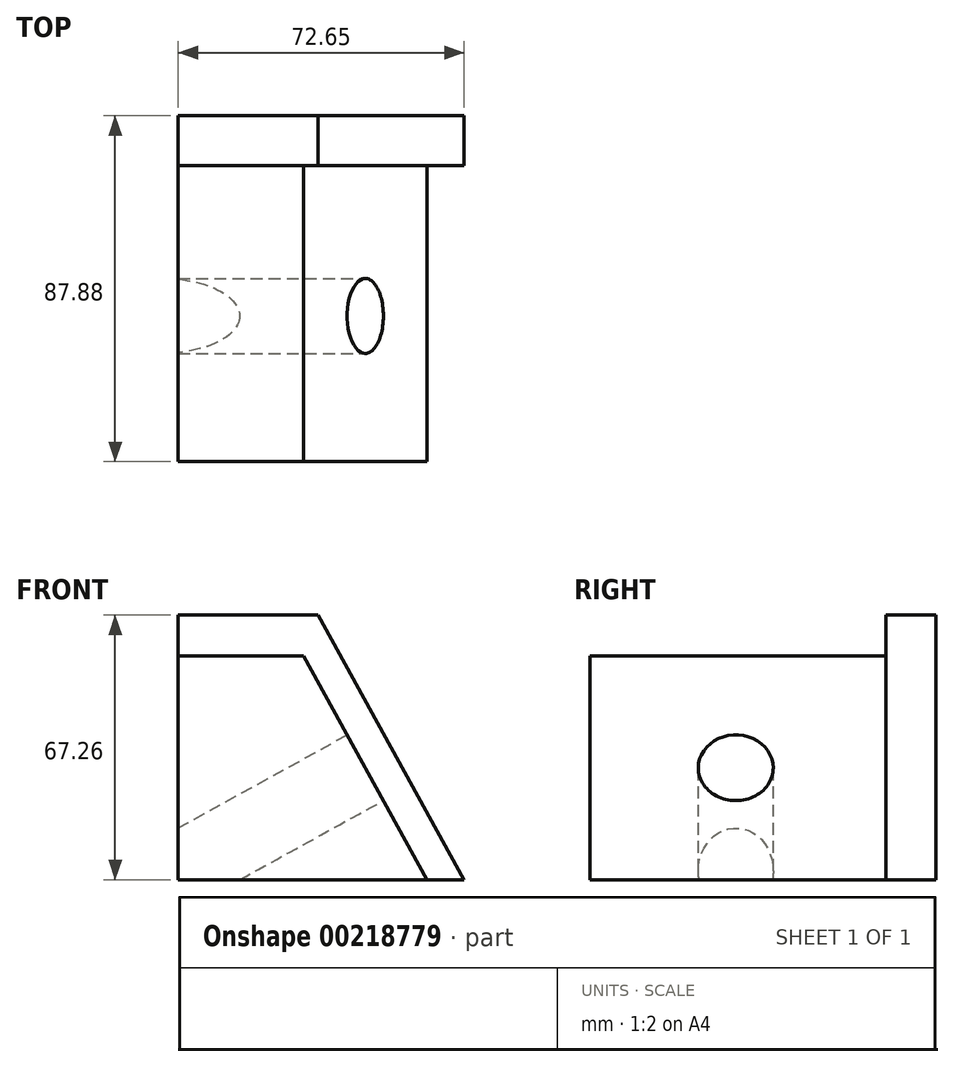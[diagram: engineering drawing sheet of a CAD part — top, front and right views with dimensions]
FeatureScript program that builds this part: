
annotation { "Feature Type Name" : "Feature", "Feature Type Description" : "" }
export const myFeature = defineFeature(function(context is Context, id is Id, definition is map)
    precondition{}
    {
        {
            var Q0;
            Q0=qCreatedBy(makeId("Front.planeOp"),FACE);
            var sketch = newSketch(context, id + "F0", { "sketchPlane" : qUnion([Q0])});
            skPoint(sketch, "E0.middle", {"position": v(0, 0) * mm});
            skLineSegment(sketch, "E1", {"start": v(-86.8, 0) * mm, "end": v(-86.8, 67.26) * mm});
            skLineSegment(sketch, "E2", {"start": v(-86.8, 67.26) * mm, "end": v(-51.25, 67.26) * mm});
            skLineSegment(sketch, "E3", {"start": v(-51.25, 67.26) * mm, "end": v(-14.16, 0) * mm});
            skLineSegment(sketch, "E4", {"start": v(-14.16, 0) * mm, "end": v(-86.8, 0) * mm});
            skSolve(sketch);
        }
        {
            var Q0;
            Q0=makeQuery(id+"F0.imprint","IMPRINT",FACE,{"disambiguationData":[TD([[makeQuery(id+"F0.imprint","IMPRINT",EDGE,{"derivedFrom":sQuery(id+"F0.wireOp",EDGE,"E1")}),-1.0]])]});
            extrude(context, id + "F1", {"entities" : qUnion([Q0]), "depth" : 12.7 * mm});
        }
        {
            var Q0;
            Q0=makeQuery(id+"F1.opExtrude","CAP_FACE",FACE,{"disambiguationData":[OSD([sQuery(id+"F0.wireOp",EDGE,"E1"),sQuery(id+"F0.wireOp",EDGE,"E2"),sQuery(id+"F0.wireOp",EDGE,"E3"),sQuery(id+"F0.wireOp",EDGE,"E4")])],"isStart":false});
            var sketch = newSketch(context, id + "F2", { "sketchPlane" : qUnion([Q0])});
            skLineSegment(sketch, "E5", {"start": v(-86.8, 56.94) * mm, "end": v(-86.8, 0) * mm});
            skLineSegment(sketch, "E6", {"start": v(-86.8, 0) * mm, "end": v(-23.59, 0) * mm});
            skLineSegment(sketch, "E7", {"start": v(-86.8, 56.94) * mm, "end": v(-54.98, 56.94) * mm});
            skLineSegment(sketch, "E8", {"start": v(-54.98, 56.94) * mm, "end": v(-23.59, 0) * mm});
            skSolve(sketch);
        }
        {
            var Q0;
            Q0=makeQuery(id+"F2.imprint","IMPRINT",FACE,{"disambiguationData":[TD([[makeQuery(id+"F2.imprint","IMPRINT",EDGE,{"derivedFrom":sQuery(id+"F2.wireOp",EDGE,"E5")}),-1.0]])]});
            extrude(context, id + "F3", {"entities" : qUnion([Q0]), "operationType" : NewBodyOperationType.ADD, "depth" : 75.18 * mm});
        }
        {
            var Q0;
            Q0=makeQuery(id+"F3.opExtrude","SWEPT_FACE",FACE,{"disambiguationData":[OSD([sQuery(id+"F2.wireOp",EDGE,"E8")])]});
            var sketch = newSketch(context, id + "F4", { "sketchPlane" : qUnion([Q0])});
            skCircle(sketch, "E9", {"center": v(-50.87, 43.9) * mm, "radius": 9.56 * mm});
            skPoint(sketch, "E9.centerSnap0", {"position": v(-87.88, 43.9) * mm});
            skSolve(sketch);
        }
        {
            var Q0;
            Q0=sQuery(id+"F4.wireOp",VERTEX,"E9.center");
            var Q1;
            Q1=makeQuery(id+"F1.opExtrude","SWEPT_BODY",BODY,{"disambiguationData":[OSD([sQuery(id+"F0.wireOp",EDGE,"E1"),sQuery(id+"F0.wireOp",EDGE,"E2"),sQuery(id+"F0.wireOp",EDGE,"E3"),sQuery(id+"F0.wireOp",EDGE,"E4")])]});
            hole(context, id + "F5", {"style" : HoleStyle.SIMPLE, "endStyle" : HoleEndStyle.THROUGH, "holeDiameter" : 19.05 * mm, "locations" : qUnion([Q0]), "scope" : qUnion([Q1]), "isTappedThrough" : true});
        }
    });
